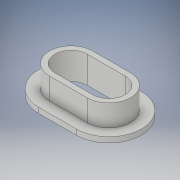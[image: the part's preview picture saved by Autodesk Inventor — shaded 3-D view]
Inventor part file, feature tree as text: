
AUTODESK INVENTOR PART (.ipt)
format: ipt  version: 2017 (Build 210142000, 142)  size: 264,704 bytes
history: native  units: mm
features: extrude x3, sketch x3, projected_geometry x2, other x1
ambient origin geometry x8: Origin, YZ Plane, XZ Plane, XY Plane, X Axis, Y Axis, Z Axis, Center Point
bodies: Body1 (feature_tree)
feature tree (9):
  other  "Твердое тело1"
  extrude  "Выдавливание1"  Depth=7.0mm
  extrude  "Выдавливание2"  Depth=8.0mm
  extrude  "Выдавливание3"  Depth=5.0mm TaperAngle=0.0deg
  sketch  "Эскиз1"
  sketch  "Эскиз2"
  projected_geometry  "Спроецированная петля1"
  sketch  "Эскиз3"
  projected_geometry  "Спроецированная петля2"
